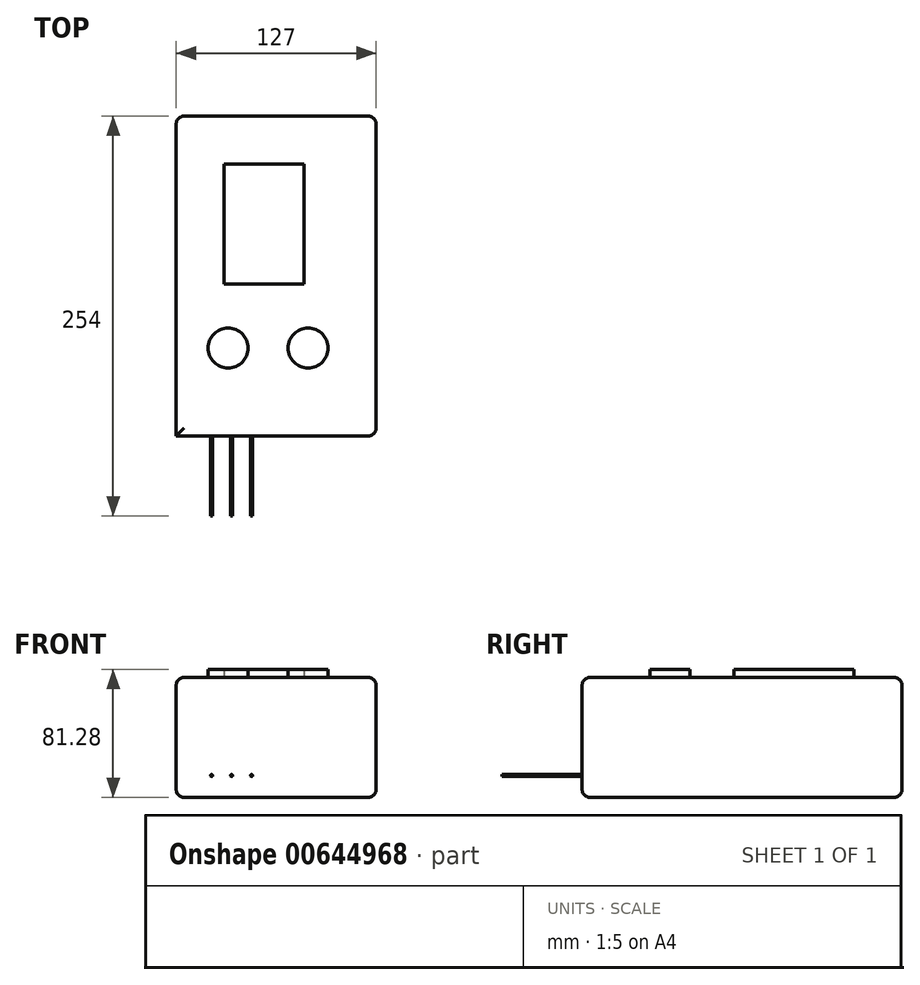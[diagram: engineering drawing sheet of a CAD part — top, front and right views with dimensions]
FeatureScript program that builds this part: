
annotation { "Feature Type Name" : "Feature", "Feature Type Description" : "" }
export const myFeature = defineFeature(function(context is Context, id is Id, definition is map)
    precondition{}
    {
        {
            var Q0;
            Q0=qCreatedBy(makeId("Front.planeOp"),FACE);
            var sketch = newSketch(context, id + "F0", { "sketchPlane" : qUnion([Q0])});
            skLineSegment(sketch, "E0.bottom", {"start": v(0, 0) * mm, "end": v(127, 0) * mm});
            skLineSegment(sketch, "E0.top", {"start": v(0, 76.2) * mm, "end": v(127, 76.2) * mm});
            skLineSegment(sketch, "E0.left", {"start": v(0, 0) * mm, "end": v(0, 76.2) * mm});
            skLineSegment(sketch, "E0.right", {"start": v(127, 0) * mm, "end": v(127, 76.2) * mm});
            skSolve(sketch);
        }
        {
            var Q0;
            Q0 = qSketchRegion(id + "F0", true);
            extrude(context, id + "F1", {"entities" : qUnion([Q0]), "depth" : 203.2 * mm, "offsetDistance" : 25.4 * mm});
        }
        {
            var Q0;
            Q0=makeQuery(id+"F1.opExtrude","CAP_EDGE",EDGE,{"disambiguationData":[OSD([sQuery(id+"F0.wireOp",EDGE,"E0.top")])],"isStart":false});
            var Q1;
            Q1=makeQuery(id+"F1.opExtrude","SWEPT_EDGE",EDGE,{"disambiguationData":[OSD([sQuery(id+"F0.wireOp",EDGE,"E0.top"),sQuery(id+"F0.wireOp",EDGE,"E0.right")])]});
            var Q2;
            Q2=makeQuery(id+"F1.opExtrude","CAP_EDGE",EDGE,{"disambiguationData":[OSD([sQuery(id+"F0.wireOp",EDGE,"E0.right")])],"isStart":false});
            var Q3;
            Q3=makeQuery(id+"F1.opExtrude","CAP_EDGE",EDGE,{"disambiguationData":[OSD([sQuery(id+"F0.wireOp",EDGE,"E0.right")])],"isStart":true});
            var Q4;
            Q4=makeQuery(id+"F1.opExtrude","SWEPT_EDGE",EDGE,{"disambiguationData":[OSD([sQuery(id+"F0.wireOp",EDGE,"E0.bottom"),sQuery(id+"F0.wireOp",EDGE,"E0.right")])]});
            var Q5;
            Q5=makeQuery(id+"F1.opExtrude","CAP_EDGE",EDGE,{"disambiguationData":[OSD([sQuery(id+"F0.wireOp",EDGE,"E0.bottom")])],"isStart":false});
            var Q6;
            Q6=makeQuery(id+"F1.opExtrude","CAP_EDGE",EDGE,{"disambiguationData":[OSD([sQuery(id+"F0.wireOp",EDGE,"E0.bottom")])],"isStart":true});
            var Q7;
            Q7=makeQuery(id+"F1.opExtrude","CAP_EDGE",EDGE,{"disambiguationData":[OSD([sQuery(id+"F0.wireOp",EDGE,"E0.left")])],"isStart":true});
            var Q8;
            Q8=makeQuery(id+"F1.opExtrude","SWEPT_EDGE",EDGE,{"disambiguationData":[OSD([sQuery(id+"F0.wireOp",EDGE,"E0.bottom"),sQuery(id+"F0.wireOp",EDGE,"E0.left")])]});
            var Q9;
            Q9=makeQuery(id+"F1.opExtrude","SWEPT_EDGE",EDGE,{"disambiguationData":[OSD([sQuery(id+"F0.wireOp",EDGE,"E0.top"),sQuery(id+"F0.wireOp",EDGE,"E0.left")])]});
            var Q10;
            Q10=makeQuery(id+"F1.opExtrude","SWEPT_FACE",FACE,{"disambiguationData":[OSD([sQuery(id+"F0.wireOp",EDGE,"E0.top")])]});
            fillet(context, id + "F2", {"entities" : qUnion([Q0, Q1, Q2, Q3, Q4, Q5, Q6, Q7, Q8, Q9, Q10]), "radius" : 5.08 * mm, "tangentPropagation" : true, "allowEdgeOverflow" : false});
        }
        {
            var Q0;
            Q0=makeQuery(id+"F1.opExtrude","CAP_FACE",FACE,{"disambiguationData":[OSD([sQuery(id+"F0.wireOp",EDGE,"E0.bottom"),sQuery(id+"F0.wireOp",EDGE,"E0.top"),sQuery(id+"F0.wireOp",EDGE,"E0.left"),sQuery(id+"F0.wireOp",EDGE,"E0.right")])],"isStart":false});
            var sketch = newSketch(context, id + "F3", { "sketchPlane" : qUnion([Q0])});
            skCircle(sketch, "E1", {"center": v(22.5, 13.9) * mm, "radius": 0.64 * mm});
            skCircle(sketch, "E2", {"center": v(35.2, 13.9) * mm, "radius": 0.64 * mm});
            skCircle(sketch, "E3", {"center": v(47.9, 13.9) * mm, "radius": 0.64 * mm});
            skSolve(sketch);
        }
        {
            var Q0;
            Q0 = qSketchRegion(id + "F3", true);
            extrude(context, id + "F4", {"entities" : qUnion([Q0]), "operationType" : NewBodyOperationType.ADD, "depth" : 50.8 * mm, "offsetDistance" : 25.4 * mm});
        }
        {
            var Q0;
            Q0=makeQuery(id+"F1.opExtrude","SWEPT_FACE",FACE,{"disambiguationData":[OSD([sQuery(id+"F0.wireOp",EDGE,"E0.top")])]});
            var sketch = newSketch(context, id + "F5", { "sketchPlane" : qUnion([Q0])});
            skLineSegment(sketch, "E4.bottom", {"start": v(81.28, -30.48) * mm, "end": v(30.48, -30.48) * mm});
            skLineSegment(sketch, "E4.top", {"start": v(81.28, -106.68) * mm, "end": v(30.48, -106.68) * mm});
            skLineSegment(sketch, "E4.left", {"start": v(81.28, -30.48) * mm, "end": v(81.28, -106.68) * mm});
            skLineSegment(sketch, "E4.right", {"start": v(30.48, -30.48) * mm, "end": v(30.48, -106.68) * mm});
            skCircle(sketch, "E5", {"center": v(33.02, -147.32) * mm, "radius": 12.7 * mm});
            skCircle(sketch, "E6", {"center": v(83.82, -147.32) * mm, "radius": 12.7 * mm});
            skSolve(sketch);
        }
        {
            var Q0;
            Q0 = qSketchRegion(id + "F5", true);
            extrude(context, id + "F6", {"entities" : qUnion([Q0]), "operationType" : NewBodyOperationType.ADD, "depth" : 5.08 * mm, "offsetDistance" : 25.4 * mm});
        }
    });
